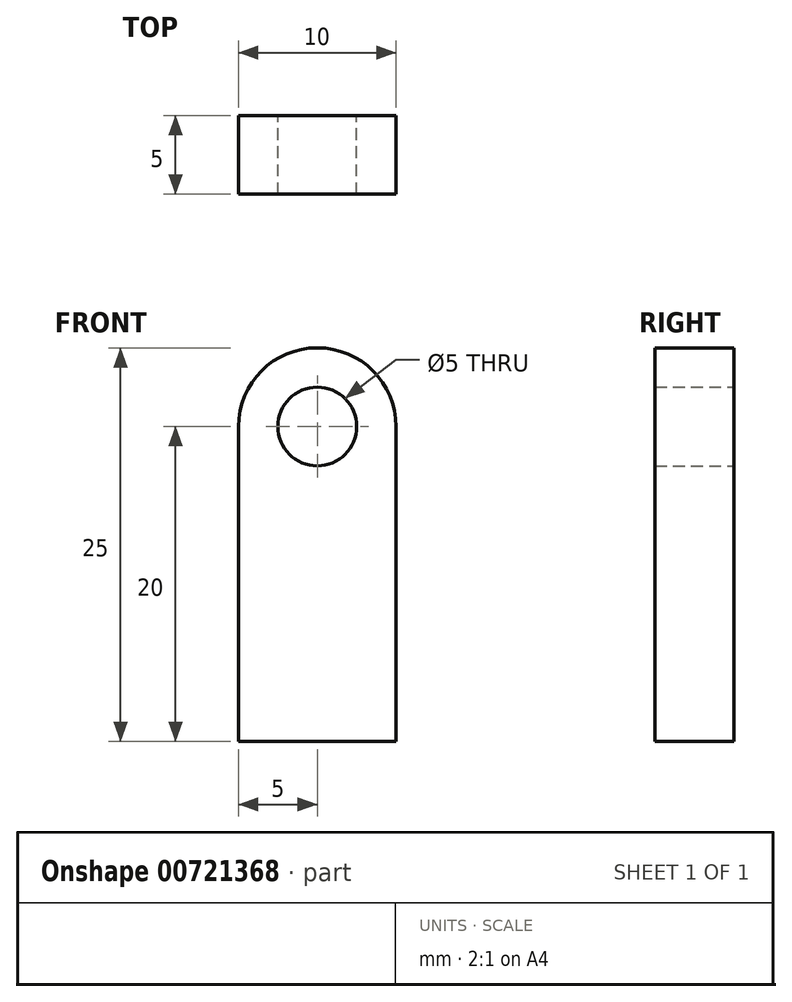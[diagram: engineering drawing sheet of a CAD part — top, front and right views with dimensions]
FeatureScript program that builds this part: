
annotation { "Feature Type Name" : "Feature", "Feature Type Description" : "" }
export const myFeature = defineFeature(function(context is Context, id is Id, definition is map)
    precondition{}
    {
        {
            var Q0;
            Q0=qCreatedBy(makeId("Front.planeOp"),FACE);
            var sketch = newSketch(context, id + "F0", { "sketchPlane" : qUnion([Q0])});
            skLineSegment(sketch, "E0.top", {"start": v(5, -10) * mm, "end": v(-5, -10) * mm});
            skLineSegment(sketch, "E0.left", {"start": v(5, 10) * mm, "end": v(5, -10) * mm});
            skLineSegment(sketch, "E0.right", {"start": v(-5, 10) * mm, "end": v(-5, -10) * mm});
            skPoint(sketch, "E0.middle", {"position": v(0, 0) * mm});
            skArc(sketch, "E1", {"start": v(5, 10) * mm, "mid": v(0, 15) * mm, "end": v(-5, 10) * mm});
            skCircle(sketch, "E2", {"center": v(0, 10) * mm, "radius": 2.5 * mm});
            skSolve(sketch);
        }
        {
            var Q0;
            Q0 = qSketchRegion(id + "F0", true);
            extrude(context, id + "F1", {"entities" : qUnion([Q0]), "depth" : 5 * mm, "offsetDistance" : 25.4 * mm});
        }
    });
